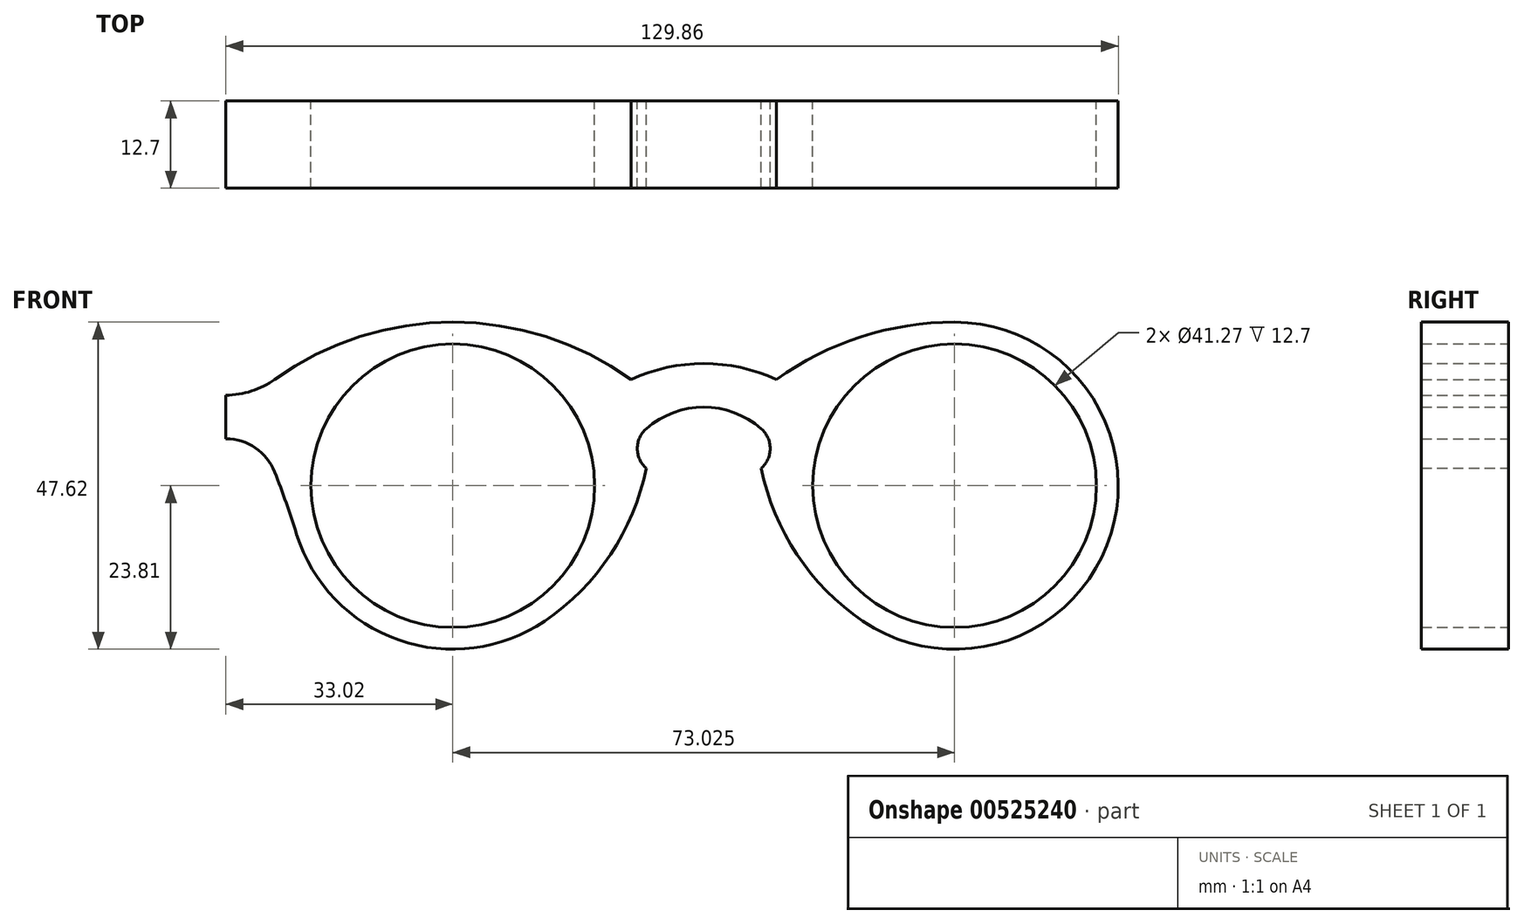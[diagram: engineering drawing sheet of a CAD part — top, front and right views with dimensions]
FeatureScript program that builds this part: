
annotation { "Feature Type Name" : "Feature", "Feature Type Description" : "" }
export const myFeature = defineFeature(function(context is Context, id is Id, definition is map)
    precondition{}
    {
        {
            var Q0;
            Q0=qCreatedBy(makeId("Front.planeOp"),FACE);
            var sketch = newSketch(context, id + "F0", { "sketchPlane" : qUnion([Q0])});
            skCircle(sketch, "E0", {"center": v(0, 0) * mm, "radius": 20.64 * mm});
            skCircle(sketch, "E1", {"center": v(73.03, 0) * mm, "radius": 20.64 * mm});
            skCircle(sketch, "E2", {"center": v(0, 0) * mm, "radius": 23.81 * mm});
            skCircle(sketch, "E3", {"center": v(73.03, 0) * mm, "radius": 23.81 * mm});
            skArc(sketch, "E4", {"start": v(25.93, 15.47) * mm, "mid": v(13.62, 21.68) * mm, "end": v(0, 23.81) * mm});
            skArc(sketch, "E5", {"start": v(73.03, 23.81) * mm, "mid": v(59.4, 21.68) * mm, "end": v(47.1, 15.47) * mm});
            skArc(sketch, "E6", {"start": v(47.1, 15.47) * mm, "mid": v(36.51, 17.78) * mm, "end": v(25.93, 15.47) * mm});
            skArc(sketch, "E7", {"start": v(13.36, -19.71) * mm, "mid": v(22.94, -10.04) * mm, "end": v(28.14, 2.54) * mm});
            skArc(sketch, "E8", {"start": v(28.14, 8.28) * mm, "mid": v(26.84, 5.41) * mm, "end": v(28.14, 2.54) * mm});
            skArc(sketch, "E9", {"start": v(44.88, 8.28) * mm, "mid": v(36.51, 11.43) * mm, "end": v(28.14, 8.28) * mm});
            skArc(sketch, "E10", {"start": v(0, 23.81) * mm, "mid": v(-13.62, 21.68) * mm, "end": v(-25.93, 15.47) * mm});
            skArc(sketch, "E11", {"start": v(44.88, 2.54) * mm, "mid": v(46.18, 5.41) * mm, "end": v(44.88, 8.28) * mm});
            skArc(sketch, "E12", {"start": v(44.88, 2.54) * mm, "mid": v(50.08, -10.04) * mm, "end": v(59.66, -19.71) * mm});
            skArc(sketch, "E13", {"start": v(-33.02, 13.19) * mm, "mid": v(-29.3, 13.77) * mm, "end": v(-25.93, 15.47) * mm});
            skArc(sketch, "E14", {"start": v(-25.93, 2) * mm, "mid": v(-24.25, -2.52) * mm, "end": v(-22.73, -7.09) * mm});
            skLineSegment(sketch, "E15", {"start": v(-33.02, 13.19) * mm, "end": v(-33.02, 6.84) * mm});
            skArc(sketch, "E16", {"start": v(-25.93, 2) * mm, "mid": v(-28.73, 5.51) * mm, "end": v(-33.02, 6.84) * mm});
            skLineSegment(sketch, "E17", {"start": v(-33.02, 6.84) * mm, "end": v(-39.58, 6.84) * mm, "construction": true});
            skLineSegment(sketch, "E18", {"start": v(36.51, -7.62) * mm, "end": v(36.51, 17.78) * mm, "construction": true});
            skArc(sketch, "E19.MirrorCS", {"start": v(98.95, 2) * mm, "mid": v(101.75, 5.51) * mm, "end": v(106.04, 6.84) * mm});
            skArc(sketch, "E20.MirrorCS", {"start": v(98.95, 2) * mm, "mid": v(97.27, -2.52) * mm, "end": v(95.76, -7.09) * mm});
            skArc(sketch, "E21.MirrorCS", {"start": v(106.04, 13.19) * mm, "mid": v(102.32, 13.77) * mm, "end": v(98.95, 15.47) * mm});
            skArc(sketch, "E22.MirrorCS", {"start": v(73.02, 23.81) * mm, "mid": v(86.64, 21.68) * mm, "end": v(98.95, 15.47) * mm});
            skLineSegment(sketch, "E23.MirrorCS", {"start": v(106.04, 13.19) * mm, "end": v(106.04, 6.84) * mm});
            skSolve(sketch);
        }
        {
            var Q0;
            {var subQ1=sQuery(id+"F0.wireOp",EDGE,"E4");Q0=makeQuery(id+"F0.imprint","IMPRINT",FACE,{"disambiguationData":[TD([[makeQuery(id+"F0.imprint","IMPRINT",EDGE,{"derivedFrom":subQ1}),1.0]])]});}
            var Q1;
            Q1=makeQuery(id+"F0.imprint","IMPRINT",FACE,{"disambiguationData":[TD([[makeQuery(id+"F0.imprint","IMPRINT",EDGE,{"derivedFrom":sQuery(id+"F0.wireOp",EDGE,"E0")}),-1.0]])]});
            var Q2;
            {var subQ0=sQuery(id+"F0.wireOp",EDGE,"E10");Q2=makeQuery(id+"F0.imprint","IMPRINT",FACE,{"disambiguationData":[TD([[makeQuery(id+"F0.imprint","IMPRINT",EDGE,{"derivedFrom":subQ0}),1.0]])]});}
            var Q3;
            Q3=makeQuery(id+"F0.imprint","IMPRINT",FACE,{"disambiguationData":[TD([[makeQuery(id+"F0.imprint","IMPRINT",EDGE,{"derivedFrom":sQuery(id+"F0.wireOp",EDGE,"E1")}),-1.0]])]});
            var Q4;
            Q4=makeQuery(id+"F0.imprint","IMPRINT",FACE,{"disambiguationData":[TD([[makeQuery(id+"F0.imprint","IMPRINT",EDGE,{"derivedFrom":sQuery(id+"F0.wireOp",EDGE,"E19.MirrorCS")}),1.0]])]});
            extrude(context, id + "F1", {"entities" : qUnion([Q0, Q1, Q2, Q3, Q4]), "depth" : 12.7 * mm, "offsetDistance" : 25.4 * mm});
        }
    });
